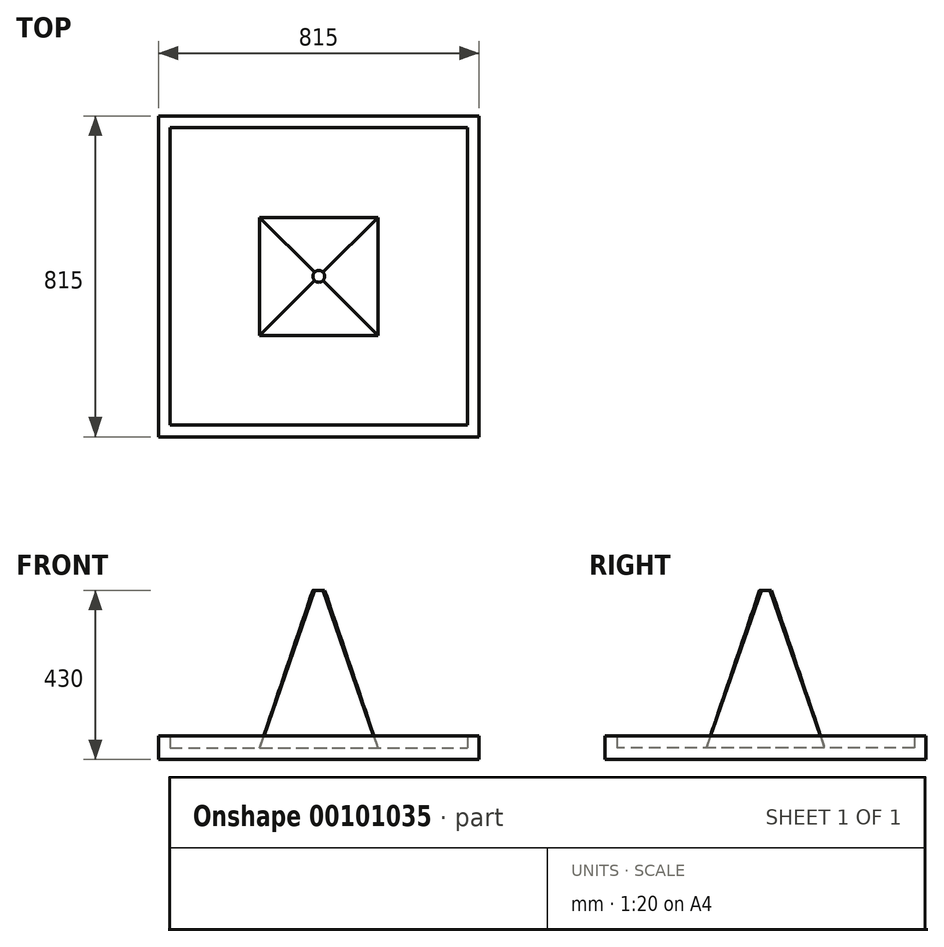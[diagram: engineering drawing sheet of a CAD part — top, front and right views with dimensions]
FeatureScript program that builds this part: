
annotation { "Feature Type Name" : "Feature", "Feature Type Description" : "" }
export const myFeature = defineFeature(function(context is Context, id is Id, definition is map)
    precondition{}
    {
        {
            var Q0;
            Q0=qCreatedBy(makeId("Top.planeOp"),FACE);
            var sketch = newSketch(context, id + "F0", { "sketchPlane" : qUnion([Q0])});
            skLineSegment(sketch, "E0.bottom", {"start": v(-377.5, 377.5) * mm, "end": v(377.5, 377.5) * mm});
            skLineSegment(sketch, "E0.top", {"start": v(-377.5, -377.5) * mm, "end": v(377.5, -377.5) * mm});
            skLineSegment(sketch, "E0.left", {"start": v(-377.5, 377.5) * mm, "end": v(-377.5, -377.5) * mm});
            skLineSegment(sketch, "E0.right", {"start": v(377.5, 377.5) * mm, "end": v(377.5, -377.5) * mm});
            skLineSegment(sketch, "E1.bottom", {"start": v(-407.5, 407.5) * mm, "end": v(407.5, 407.5) * mm});
            skLineSegment(sketch, "E1.top", {"start": v(-407.5, -407.5) * mm, "end": v(407.5, -407.5) * mm});
            skLineSegment(sketch, "E1.left", {"start": v(-407.5, 407.5) * mm, "end": v(-407.5, -407.5) * mm});
            skLineSegment(sketch, "E1.right", {"start": v(407.5, 407.5) * mm, "end": v(407.5, -407.5) * mm});
            skLineSegment(sketch, "E2.bottom", {"start": v(-150, 150) * mm, "end": v(150, 150) * mm});
            skLineSegment(sketch, "E2.top", {"start": v(-150, -150) * mm, "end": v(150, -150) * mm});
            skLineSegment(sketch, "E2.left", {"start": v(-150, 150) * mm, "end": v(-150, -150) * mm});
            skLineSegment(sketch, "E2.right", {"start": v(150, 150) * mm, "end": v(150, -150) * mm});
            skLineSegment(sketch, "E3", {"start": v(0, 150) * mm, "end": v(0, 377.5) * mm, "construction": true});
            skLineSegment(sketch, "E4", {"start": v(0, -150) * mm, "end": v(0, -377.5) * mm, "construction": true});
            skLineSegment(sketch, "E5", {"start": v(-150, 0) * mm, "end": v(-377.5, 0) * mm, "construction": true});
            skLineSegment(sketch, "E6", {"start": v(150, 0) * mm, "end": v(377.5, 0) * mm, "construction": true});
            skSolve(sketch);
        }
        {
            var Q0;
            Q0=makeQuery(id+"F0.imprint","IMPRINT",FACE,{"disambiguationData":[TD([[makeQuery(id+"F0.imprint","IMPRINT",EDGE,{"derivedFrom":sQuery(id+"F0.wireOp",EDGE,"E2.bottom")}),-1.0]])]});
            var Q1;
            Q1=makeQuery(id+"F0.imprint","IMPRINT",FACE,{"disambiguationData":[TD([[makeQuery(id+"F0.imprint","IMPRINT",EDGE,{"derivedFrom":sQuery(id+"F0.wireOp",EDGE,"E0.bottom")}),-1.0]])]});
            extrude(context, id + "F1", {"entities" : qUnion([Q0, Q1]), "depth" : 30 * mm});
        }
        {
            var Q0;
            Q0=makeQuery(id+"F0.imprint","IMPRINT",FACE,{"disambiguationData":[TD([[makeQuery(id+"F0.imprint","IMPRINT",EDGE,{"derivedFrom":sQuery(id+"F0.wireOp",EDGE,"E0.bottom")}),1.0]])]});
            extrude(context, id + "F2", {"entities" : qUnion([Q0]), "operationType" : NewBodyOperationType.ADD, "depth" : 60 * mm});
        }
        {
            var Q0;
            Q0=makeQuery(id+"F1.opExtrude","CAP_FACE",FACE,{"disambiguationData":[OSD([sQuery(id+"F0.wireOp",EDGE,"E0.bottom"),sQuery(id+"F0.wireOp",EDGE,"E0.top"),sQuery(id+"F0.wireOp",EDGE,"E0.left"),sQuery(id+"F0.wireOp",EDGE,"E0.right")])],"isStart":false});
            cPlane(context, id + "F3", {"entities" : qUnion([Q0]), "cplaneType" : CPlaneType.OFFSET, "offset" : 400 * mm, "width" : 150 * mm, "height" : 150 * mm});
        }
        {
            var Q0;
            Q0=makeQuery(id+"F1.opExtrude","CAP_FACE",FACE,{"disambiguationData":[OSD([sQuery(id+"F0.wireOp",EDGE,"E0.bottom"),sQuery(id+"F0.wireOp",EDGE,"E0.top"),sQuery(id+"F0.wireOp",EDGE,"E0.left"),sQuery(id+"F0.wireOp",EDGE,"E0.right")])],"isStart":false});
            var sketch = newSketch(context, id + "F4", { "sketchPlane" : qUnion([Q0])});
            skLineSegment(sketch, "E7.bottom", {"start": v(-150, 150) * mm, "end": v(150, 150) * mm});
            skLineSegment(sketch, "E7.top", {"start": v(-150, -150) * mm, "end": v(150, -150) * mm});
            skLineSegment(sketch, "E7.left", {"start": v(-150, 150) * mm, "end": v(-150, -150) * mm});
            skLineSegment(sketch, "E7.right", {"start": v(150, 150) * mm, "end": v(150, -150) * mm});
            skSolve(sketch);
        }
        {
            var Q0;
            Q0=qCreatedBy(id+"F3.planeOp",FACE);
            var sketch = newSketch(context, id + "F5", { "sketchPlane" : qUnion([Q0])});
            skPoint(sketch, "E8", {"position": v(0, 0) * mm});
            skCircle(sketch, "E9", {"center": v(0, 0) * mm, "radius": 15.02 * mm});
            skSolve(sketch);
        }
        {
            var Q1;
            Q1=makeQuery(id+"F4.imprint","IMPRINT",FACE,{"disambiguationData":[TD([[makeQuery(id+"F4.imprint","IMPRINT",EDGE,{"derivedFrom":sQuery(id+"F4.wireOp",EDGE,"E7.bottom")}),-1.0]])]});
            var Q2;
            Q2=makeQuery(id+"F5.imprint","IMPRINT",FACE,{"disambiguationData":[TD([[makeQuery(id+"F5.imprint","IMPRINT",EDGE,{"derivedFrom":sQuery(id+"F5.wireOp",EDGE,"E9")}),1.0]])]});
            loft(context, id + "F6", {"operationType" : NewBodyOperationType.ADD, "sheetProfilesArray" : [{ "sheetProfileEntities" : qUnion([Q1]) }, { "sheetProfileEntities" : qUnion([Q2]) }]});
        }
    });
